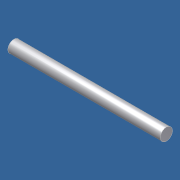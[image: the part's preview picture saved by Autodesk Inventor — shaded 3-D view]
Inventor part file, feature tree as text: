
AUTODESK INVENTOR PART (.ipt)
format: ipt  version: unknown  size: 157,696 bytes
history: native  units: in
note: dims shown in document units (in); Inventor stores cm internally (conversion verified against a paired STEP export)
features: revolve x1, sketch x1
ambient origin geometry x8: Origin, YZ Plane, XZ Plane, XY Plane, X Axis, Y Axis, Z Axis, Center Point
bodies: Solid1 (feature_tree)
feature tree (2):
  revolve  "Revolution1"  [1 undecoded]
  sketch  "Sketch1"  dims[d0=0.75in d1=0.03in d2=90.0deg]
note: 1 required parameter value undecoded (feature->parameter linkage not recoverable at this tier; creation-order binding heuristic only, values carry confidence <= 0.55)
